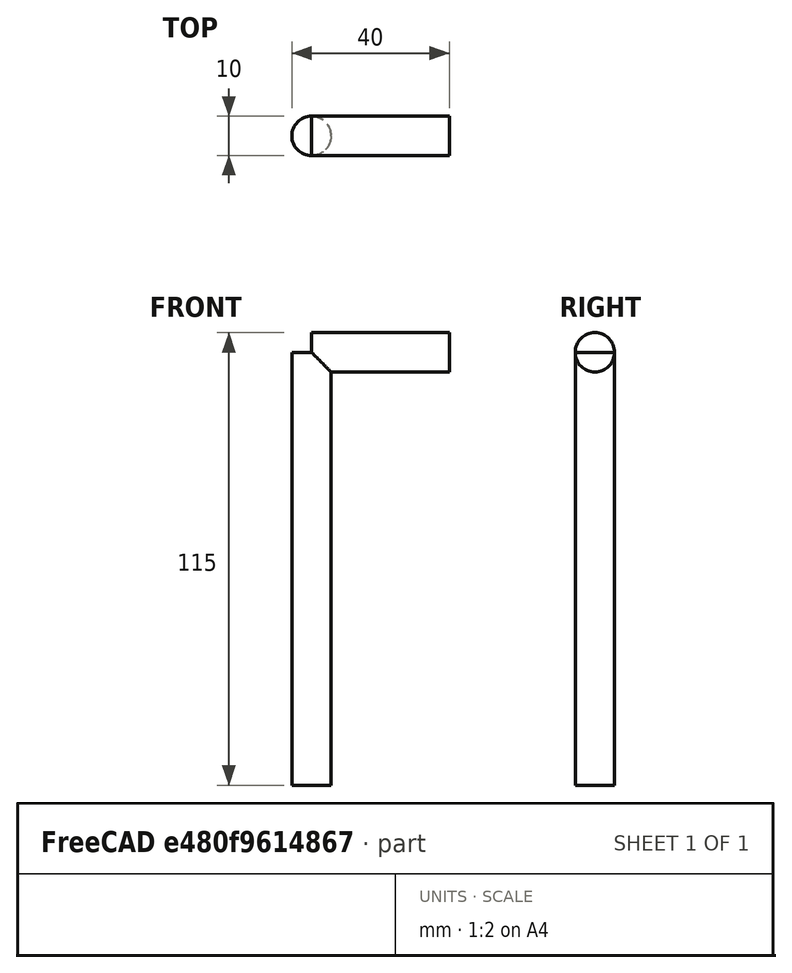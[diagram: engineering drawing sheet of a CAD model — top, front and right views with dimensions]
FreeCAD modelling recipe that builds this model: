
FCSTD DOCUMENT  (FreeCAD 0.20R29603 (Git))
Label: razor stand
License: All rights reserved
LicenseURL: http://en.wikipedia.org/wiki/All_rights_reserved
objects: PartDesign::AdditiveCylinder×2, PartDesign::Body×1
note: 5 computed .brp shape members not serialized (recipe doc carries the construction recipe); baked Part::Feature solids carry a one-line shape summary decoded from their .brp

FEATURE [PartDesign::AdditiveCylinder] Cylinder
  Angle = 360
  AttacherType = Attacher::AttachEngine3D
  FirstAngle = 0
  Height = 110
  MapMode = 5
  Radius = 5
  SecondAngle = 0
  Support = -> [XY_Plane]
FEATURE [PartDesign::AdditiveCylinder] Cylinder001
  Angle = 360
  AttacherType = Attacher::AttachEngine3D
  AttachmentOffset = pos=(0,0,0) rot=(1,0,0;1.5708rad)
  BaseFeature = -> Cylinder
  FirstAngle = 0
  Height = 35
  MapMode = 11
  Placement = pos=(0,0,110) rot=(0.57735,0.57735,0.57735;2.0944rad)
  Radius = 5
  SecondAngle = 0
  Support = -> [Cylinder]
FEATURE [PartDesign::Body] Body
  Group = -> [Cylinder,Cylinder001]
  Origin = -> Origin
  Tip = -> Cylinder001
